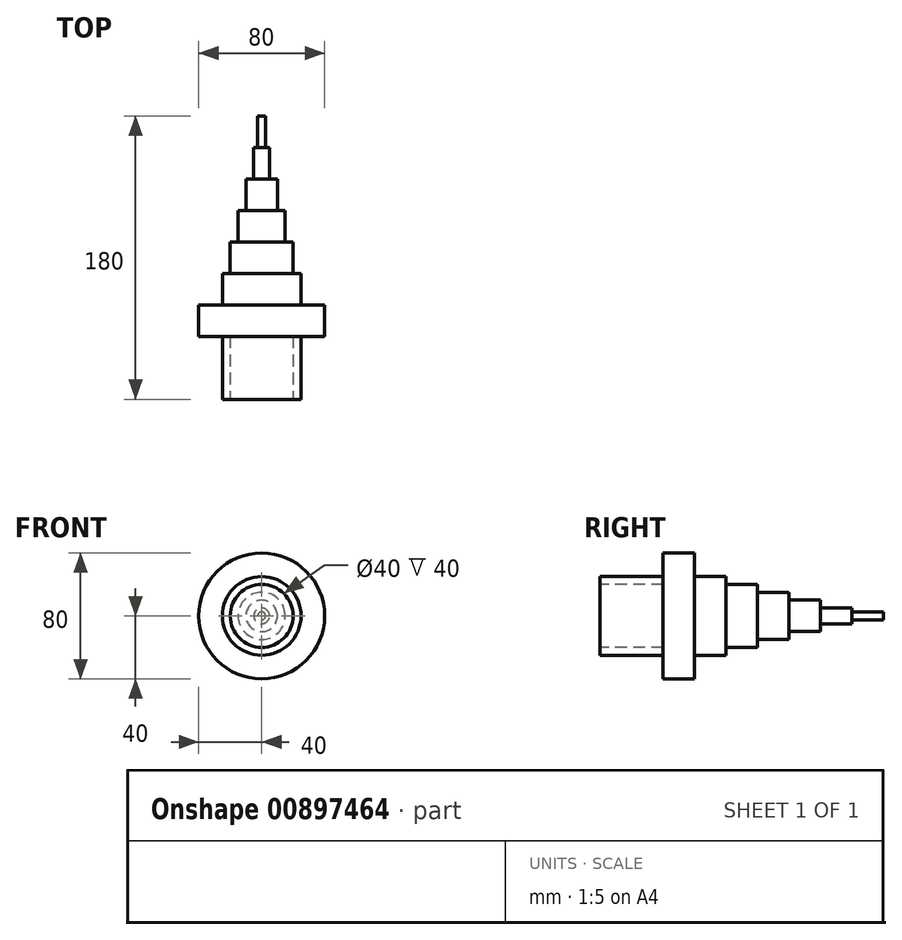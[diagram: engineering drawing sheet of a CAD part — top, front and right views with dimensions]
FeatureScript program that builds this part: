
annotation { "Feature Type Name" : "Feature", "Feature Type Description" : "" }
export const myFeature = defineFeature(function(context is Context, id is Id, definition is map)
    precondition{}
    {
        {
            var Q0;
            Q0=qCreatedBy(makeId("Front.planeOp"),FACE);
            var sketch = newSketch(context, id + "F0", { "sketchPlane" : qUnion([Q0])});
            skCircle(sketch, "E0", {"center": v(0, 0) * mm, "radius": 40 * mm});
            skSolve(sketch);
        }
        {
            var Q0;
            Q0 = qSketchRegion(id + "F0", true);
            extrude(context, id + "F1", {"entities" : qUnion([Q0]), "depth" : 20 * mm, "offsetDistance" : 25.4 * mm});
        }
        {
            var Q0;
            Q0=makeQuery(id+"F1.opExtrude","CAP_FACE",FACE,{"disambiguationData":[OSD([sQuery(id+"F0.wireOp",EDGE,"E0")])],"isStart":false});
            var sketch = newSketch(context, id + "F2", { "sketchPlane" : qUnion([Q0])});
            skCircle(sketch, "E1", {"center": v(0, 0) * mm, "radius": 25 * mm});
            skSolve(sketch);
        }
        {
            var Q0;
            Q0 = qSketchRegion(id + "F2", true);
            extrude(context, id + "F3", {"entities" : qUnion([Q0]), "operationType" : NewBodyOperationType.ADD, "depth" : 40 * mm, "offsetDistance" : 25.4 * mm});
        }
        {
            var Q0;
            Q0=makeQuery(id+"F3.opExtrude","CAP_FACE",FACE,{"disambiguationData":[OSD([sQuery(id+"F2.wireOp",EDGE,"E1")])],"isStart":false});
            var sketch = newSketch(context, id + "F4", { "sketchPlane" : qUnion([Q0])});
            skCircle(sketch, "E2", {"center": v(0, 0) * mm, "radius": 20 * mm});
            skSolve(sketch);
        }
        {
            var Q0;
            Q0 = qSketchRegion(id + "F4", true);
            extrude(context, id + "F5", {"entities" : qUnion([Q0]), "operationType" : NewBodyOperationType.REMOVE, "oppositeDirection" : true, "depth" : 40 * mm, "offsetDistance" : 25.4 * mm});
        }
        {
            var Q0;
            Q0=makeQuery(id+"F1.opExtrude","CAP_FACE",FACE,{"disambiguationData":[OSD([sQuery(id+"F0.wireOp",EDGE,"E0")])],"isStart":true});
            var sketch = newSketch(context, id + "F6", { "sketchPlane" : qUnion([Q0])});
            skCircle(sketch, "E3", {"center": v(0, 0) * mm, "radius": 25 * mm});
            skSolve(sketch);
        }
        {
            var Q0;
            Q0 = qSketchRegion(id + "F6", true);
            extrude(context, id + "F7", {"entities" : qUnion([Q0]), "operationType" : NewBodyOperationType.ADD, "depth" : 20 * mm, "offsetDistance" : 25.4 * mm});
        }
        {
            var Q0;
            Q0=makeQuery(id+"F7.opExtrude","CAP_FACE",FACE,{"disambiguationData":[OSD([sQuery(id+"F6.wireOp",EDGE,"E3")])],"isStart":false});
            var sketch = newSketch(context, id + "F8", { "sketchPlane" : qUnion([Q0])});
            skCircle(sketch, "E4", {"center": v(0, 0) * mm, "radius": 20 * mm});
            skSolve(sketch);
        }
        {
            var Q0;
            Q0 = qSketchRegion(id + "F8", true);
            extrude(context, id + "F9", {"entities" : qUnion([Q0]), "operationType" : NewBodyOperationType.ADD, "depth" : 20 * mm, "offsetDistance" : 25.4 * mm});
        }
        {
            var Q0;
            Q0=makeQuery(id+"F9.opExtrude","CAP_FACE",FACE,{"disambiguationData":[OSD([sQuery(id+"F8.wireOp",EDGE,"E4")])],"isStart":false});
            var sketch = newSketch(context, id + "F10", { "sketchPlane" : qUnion([Q0])});
            skCircle(sketch, "E5", {"center": v(0, 0) * mm, "radius": 15 * mm});
            skSolve(sketch);
        }
        {
            var Q0;
            Q0 = qSketchRegion(id + "F10", true);
            extrude(context, id + "F11", {"entities" : qUnion([Q0]), "operationType" : NewBodyOperationType.ADD, "depth" : 20 * mm, "offsetDistance" : 25.4 * mm});
        }
        {
            var Q0;
            Q0=makeQuery(id+"F11.opExtrude","CAP_FACE",FACE,{"disambiguationData":[OSD([sQuery(id+"F10.wireOp",EDGE,"E5")])],"isStart":false});
            var sketch = newSketch(context, id + "F12", { "sketchPlane" : qUnion([Q0])});
            skCircle(sketch, "E6", {"center": v(0, 0) * mm, "radius": 10 * mm});
            skSolve(sketch);
        }
        {
            var Q0;
            Q0 = qSketchRegion(id + "F12", true);
            extrude(context, id + "F13", {"entities" : qUnion([Q0]), "operationType" : NewBodyOperationType.ADD, "depth" : 20 * mm, "offsetDistance" : 25.4 * mm});
        }
        {
            var Q0;
            Q0=makeQuery(id+"F13.opExtrude","CAP_FACE",FACE,{"disambiguationData":[OSD([sQuery(id+"F12.wireOp",EDGE,"E6")])],"isStart":false});
            var sketch = newSketch(context, id + "F14", { "sketchPlane" : qUnion([Q0])});
            skCircle(sketch, "E7", {"center": v(0, 0) * mm, "radius": 5 * mm});
            skSolve(sketch);
        }
        {
            var Q0;
            Q0 = qSketchRegion(id + "F14", true);
            extrude(context, id + "F15", {"entities" : qUnion([Q0]), "operationType" : NewBodyOperationType.ADD, "depth" : 20 * mm, "offsetDistance" : 25.4 * mm});
        }
        {
            var Q0;
            Q0=makeQuery(id+"F15.opExtrude","CAP_FACE",FACE,{"disambiguationData":[OSD([sQuery(id+"F14.wireOp",EDGE,"E7")])],"isStart":false});
            var sketch = newSketch(context, id + "F16", { "sketchPlane" : qUnion([Q0])});
            skCircle(sketch, "E8", {"center": v(0, 0) * mm, "radius": 2.5 * mm});
            skSolve(sketch);
        }
        {
            var Q0;
            Q0 = qSketchRegion(id + "F16", true);
            extrude(context, id + "F17", {"entities" : qUnion([Q0]), "operationType" : NewBodyOperationType.ADD, "depth" : 20 * mm, "offsetDistance" : 25.4 * mm});
        }
    });
